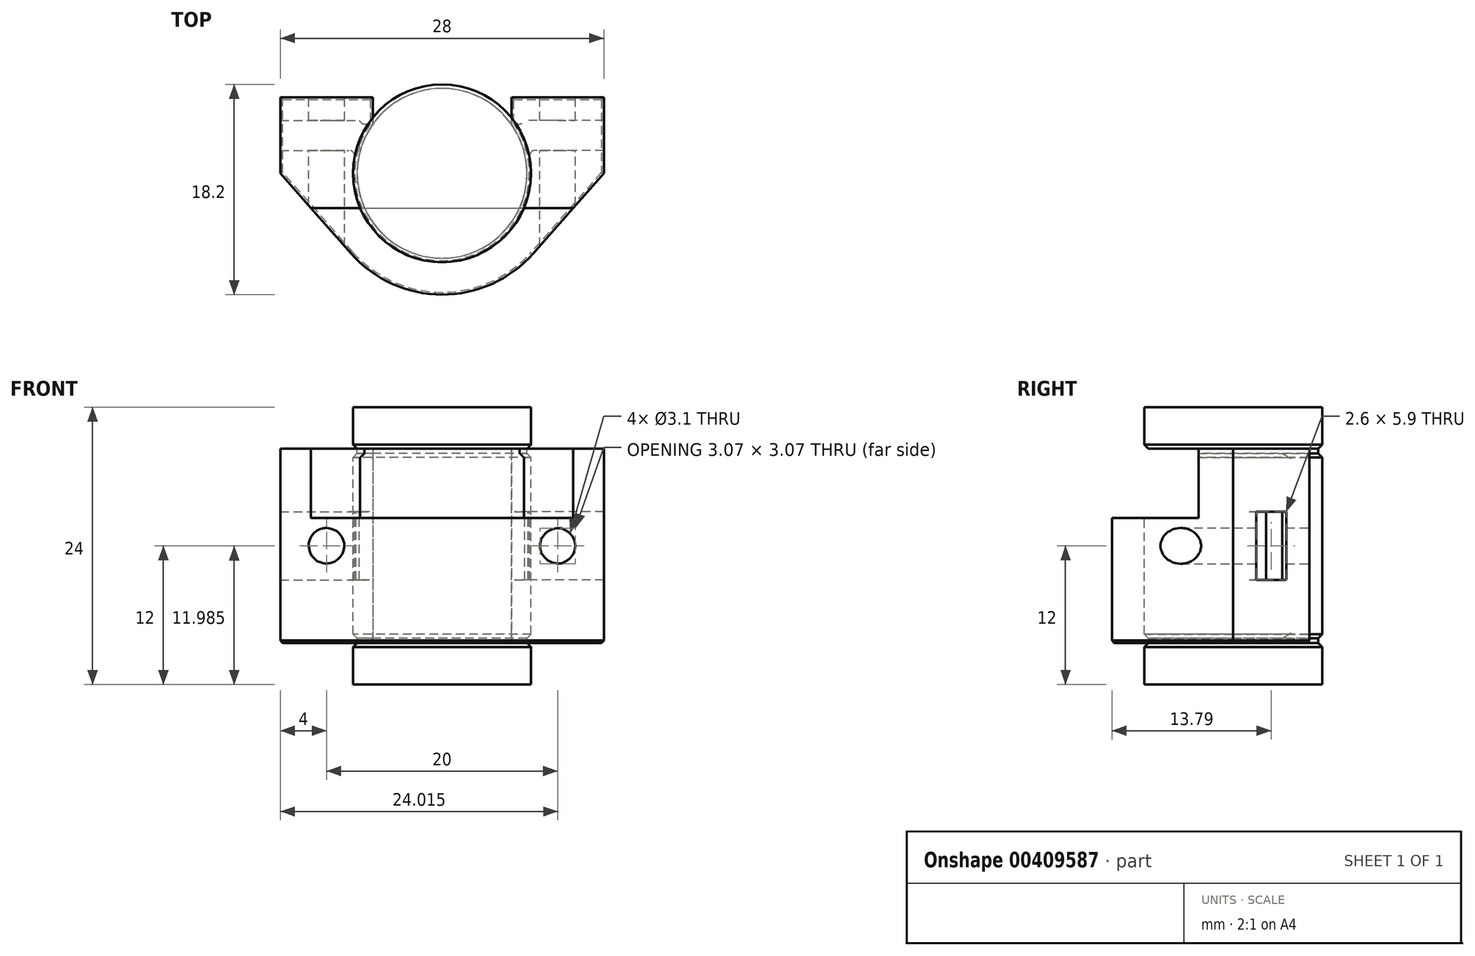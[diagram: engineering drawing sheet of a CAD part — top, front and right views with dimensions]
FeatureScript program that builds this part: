
annotation { "Feature Type Name" : "Feature", "Feature Type Description" : "" }
export const myFeature = defineFeature(function(context is Context, id is Id, definition is map)
    precondition{}
    {
        {
            var Q0;
            Q0=qCreatedBy(makeId("Front.planeOp"),FACE);
            var sketch = newSketch(context, id + "F0", { "sketchPlane" : qUnion([Q0])});
            skLineSegment(sketch, "E0", {"start": v(0, 12) * mm, "end": v(0, -12) * mm});
            skLineSegment(sketch, "E1.bottom", {"start": v(-4, 12) * mm, "end": v(-7.5, 12) * mm});
            skLineSegment(sketch, "E1.top", {"start": v(-4, -12) * mm, "end": v(-7.5, -12) * mm});
            skLineSegment(sketch, "E1.left", {"start": v(-4, 12) * mm, "end": v(-4, -12) * mm, "construction": true});
            skLineSegment(sketch, "E2", {"start": v(-7.5, 12) * mm, "end": v(-7.5, 8.75) * mm, "construction": true});
            skLineSegment(sketch, "E3", {"start": v(-7.5, 8.75) * mm, "end": v(-7.15, 8.75) * mm, "construction": true});
            skLineSegment(sketch, "E4", {"start": v(-7.15, 8.75) * mm, "end": v(-7.15, 7.65) * mm, "construction": true});
            skLineSegment(sketch, "E5", {"start": v(-7.15, 7.65) * mm, "end": v(-7.5, 7.65) * mm, "construction": true});
            skLineSegment(sketch, "E6", {"start": v(-7.5, 7.65) * mm, "end": v(-7.5, 0) * mm, "construction": true});
            skLineSegment(sketch, "E7.MirrorCS", {"start": v(-7.5, -8.75) * mm, "end": v(-7.15, -8.75) * mm, "construction": true});
            skLineSegment(sketch, "E8.MirrorCS", {"start": v(-7.15, -8.75) * mm, "end": v(-7.15, -7.65) * mm, "construction": true});
            skLineSegment(sketch, "E9.MirrorCS", {"start": v(-7.15, -7.65) * mm, "end": v(-7.5, -7.65) * mm, "construction": true});
            skLineSegment(sketch, "E10", {"start": v(-7.5, 0) * mm, "end": v(-7.5, -7.65) * mm, "construction": true});
            skLineSegment(sketch, "E11", {"start": v(-7.5, -8.75) * mm, "end": v(-7.5, -12) * mm, "construction": true});
            skLineSegment(sketch, "E12.0", {"start": v(-7.7, 12) * mm, "end": v(-7.7, 8.75) * mm});
            skLineSegment(sketch, "E13.0", {"start": v(-7.35, 8.75) * mm, "end": v(-7.35, 7.65) * mm});
            skLineSegment(sketch, "E14", {"start": v(-7.7, 8.75) * mm, "end": v(-7.35, 8.4) * mm});
            skLineSegment(sketch, "E15", {"start": v(-7.7, 7.65) * mm, "end": v(-7.7, 0) * mm});
            skLineSegment(sketch, "E16", {"start": v(-7.7, 7.65) * mm, "end": v(-7.35, 8) * mm});
            skLineSegment(sketch, "E17", {"start": v(-7.7, 12) * mm, "end": v(-7.5, 12) * mm});
            skLineSegment(sketch, "E18.MirrorCS", {"start": v(-7.7, -7.65) * mm, "end": v(-7.7, 0) * mm});
            skLineSegment(sketch, "E19.MirrorCS", {"start": v(-7.7, -7.65) * mm, "end": v(-7.35, -8) * mm});
            skLineSegment(sketch, "E20.MirrorCS", {"start": v(-7.35, -8.75) * mm, "end": v(-7.35, -7.65) * mm});
            skLineSegment(sketch, "E21.MirrorCS", {"start": v(-7.7, -8.75) * mm, "end": v(-7.35, -8.4) * mm});
            skLineSegment(sketch, "E22.MirrorCS", {"start": v(-7.7, -12) * mm, "end": v(-7.7, -8.75) * mm});
            skLineSegment(sketch, "E23.MirrorCS", {"start": v(-7.7, -12) * mm, "end": v(-7.5, -12) * mm});
            skLineSegment(sketch, "E24", {"start": v(-4, 12) * mm, "end": v(0, 12) * mm});
            skLineSegment(sketch, "E25", {"start": v(-4, -12) * mm, "end": v(0, -12) * mm});
            skSolve(sketch);
        }
        {
            var Q0;
            Q0=qCreatedBy(makeId("Top.planeOp"),FACE);
            var sketch = newSketch(context, id + "F1", { "sketchPlane" : qUnion([Q0])});
            skLineSegment(sketch, "E26", {"start": v(-5, 6.6) * mm, "end": v(5, 6.6) * mm, "construction": true});
            skCircle(sketch, "E27", {"center": v(0, 0) * mm, "radius": 7.5 * mm, "construction": true});
            skLineSegment(sketch, "E28", {"start": v(5, 6.6) * mm, "end": v(5, 5.6) * mm, "construction": true});
            skLineSegment(sketch, "E29", {"start": v(-5, 6.6) * mm, "end": v(-5, 5.6) * mm, "construction": true});
            skLineSegment(sketch, "E30", {"start": v(-5, 6.6) * mm, "end": v(-10, 6.6) * mm, "construction": true});
            skLineSegment(sketch, "E31", {"start": v(5, 6.6) * mm, "end": v(10, 6.6) * mm, "construction": true});
            skLineSegment(sketch, "E32", {"start": v(-10, 6.6) * mm, "end": v(-10, 4.6) * mm, "construction": true});
            skLineSegment(sketch, "E33.bottom", {"start": v(-12.85, 4.6) * mm, "end": v(-7.15, 4.6) * mm, "construction": true});
            skLineSegment(sketch, "E33.top", {"start": v(-12.85, 2) * mm, "end": v(-7.15, 2) * mm, "construction": true});
            skLineSegment(sketch, "E33.left", {"start": v(-12.85, 4.6) * mm, "end": v(-12.85, 2) * mm, "construction": true});
            skLineSegment(sketch, "E33.right", {"start": v(-7.15, 4.6) * mm, "end": v(-7.15, 2) * mm, "construction": true});
            skSolve(sketch);
        }
        {
            var Q0;
            Q0=qSketchRegion(id+"F0",true);
            var Q1;
            Q1=sQuery(id+"F0.wireOp",EDGE,"E0");
            revolve(context, id + "F2", {"entities" : qUnion([Q0]), "axis" : qUnion([Q1]), "revolveType" : RevolveType.FULL});
        }
        {
            var Q0;
            Q0=qCreatedBy(makeId("Top.planeOp"),FACE);
            var sketch = newSketch(context, id + "F3", { "sketchPlane" : qUnion([Q0])});
            skPoint(sketch, "E34.0", {"position": v(0, 6.6) * mm});
            skLineSegment(sketch, "E35", {"start": v(0, 6.6) * mm, "end": v(-14, 6.6) * mm, "construction": true});
            skLineSegment(sketch, "E36", {"start": v(-14, 6.6) * mm, "end": v(-14, 0) * mm});
            skLineSegment(sketch, "E37.MirrorCS", {"start": v(0, 6.6) * mm, "end": v(14, 6.6) * mm, "construction": true});
            skLineSegment(sketch, "E38.MirrorCS", {"start": v(14, 6.6) * mm, "end": v(14, 0) * mm});
            skCircle(sketch, "E39.0", {"center": v(0, 0) * mm, "radius": 7.5 * mm, "construction": true});
            skCircle(sketch, "E40.0", {"center": v(0, 0) * mm, "radius": 10.5 * mm, "construction": true});
            skArc(sketch, "E41", {"start": v(-7.88, -6.95) * mm, "mid": v(0, -10.5) * mm, "end": v(7.88, -6.95) * mm});
            skLineSegment(sketch, "E42", {"start": v(-14, 0) * mm, "end": v(-7.87, -6.95) * mm});
            skLineSegment(sketch, "E43.MirrorCS", {"start": v(14, 0) * mm, "end": v(7.87, -6.95) * mm});
            skLineSegment(sketch, "E44.0", {"start": v(-12.85, 4.6) * mm, "end": v(-7.15, 4.6) * mm, "construction": true});
            skLineSegment(sketch, "E45.0", {"start": v(-12.85, 2) * mm, "end": v(-7.15, 2) * mm, "construction": true});
            skLineSegment(sketch, "E46.0", {"start": v(-12.85, 4.6) * mm, "end": v(-12.85, 2) * mm, "construction": true});
            skLineSegment(sketch, "E47", {"start": v(-14, 6.6) * mm, "end": v(-6, 6.6) * mm});
            skLineSegment(sketch, "E48.MirrorCS", {"start": v(14, 6.6) * mm, "end": v(6, 6.6) * mm});
            skLineSegment(sketch, "E49.0", {"start": v(-7.15, 4.6) * mm, "end": v(-7.15, 2) * mm, "construction": true});
            skLineSegment(sketch, "E50", {"start": v(-6, 6.6) * mm, "end": v(-6, 3.3) * mm});
            skPoint(sketch, "E50.endSnap0", {"position": v(-7.15, 3.3) * mm});
            skLineSegment(sketch, "E51", {"start": v(-6, 3.3) * mm, "end": v(0, 3.3) * mm});
            skLineSegment(sketch, "E52.MirrorCS", {"start": v(6, 6.6) * mm, "end": v(6, 3.3) * mm});
            skLineSegment(sketch, "E53.MirrorCS", {"start": v(6, 3.3) * mm, "end": v(0, 3.3) * mm});
            skSolve(sketch);
        }
        {
            var Q0;
            Q0=qSketchRegion(id+"F3",true);
            var Q1;
            Q1=sQuery(id+"F0.wireOp",VERTEX,"E14.end");
            var Q2;
            Q2=sQuery(id+"F0.wireOp",VERTEX,"E21.MirrorCS.end");
            extrude(context, id + "F4", {"entities" : qUnion([Q0]), "endBound" : BoundingType.UP_TO_VERTEX, "endBoundEntityVertex" : qUnion([Q1]), "depth" : 25 * mm, "hasSecondDirection" : true, "secondDirectionBound" : BoundingType.UP_TO_VERTEX, "secondDirectionOppositeDirection" : true, "secondDirectionBoundEntityVertex" : qUnion([Q2]), "secondDirectionDepth" : 25 * mm});
        }
        {
            var Q0;
            Q0=makeQuery(id+"F4.opExtrude","SWEPT_FACE",FACE,{"disambiguationData":[OSD([sQuery(id+"F3.wireOp",EDGE,"E48.MirrorCS")])]});
            var sketch = newSketch(context, id + "F5", { "sketchPlane" : qUnion([Q0])});
            skPoint(sketch, "E54.0", {"position": v(-10, 0) * mm});
            skPoint(sketch, "E55.0", {"position": v(10, 0) * mm});
            skSolve(sketch);
        }
        {
            var Q0;
            Q0=makeQuery(id+"F2.opRevolve","SWEPT_BODY",BODY,{"disambiguationData":[OSD([sQuery(id+"F0.wireOp",EDGE,"E0"),sQuery(id+"F0.wireOp",EDGE,"E1.bottom"),sQuery(id+"F0.wireOp",EDGE,"E1.top"),sQuery(id+"F0.wireOp",EDGE,"E12.0"),sQuery(id+"F0.wireOp",EDGE,"E13.0"),sQuery(id+"F0.wireOp",EDGE,"E14"),sQuery(id+"F0.wireOp",EDGE,"E15"),sQuery(id+"F0.wireOp",EDGE,"E16"),sQuery(id+"F0.wireOp",EDGE,"E17"),sQuery(id+"F0.wireOp",EDGE,"E18.MirrorCS"),sQuery(id+"F0.wireOp",EDGE,"E19.MirrorCS"),sQuery(id+"F0.wireOp",EDGE,"E20.MirrorCS"),sQuery(id+"F0.wireOp",EDGE,"E21.MirrorCS"),sQuery(id+"F0.wireOp",EDGE,"E22.MirrorCS"),sQuery(id+"F0.wireOp",EDGE,"E23.MirrorCS"),sQuery(id+"F0.wireOp",EDGE,"E24"),sQuery(id+"F0.wireOp",EDGE,"E25")])]});
            var Q1;
            Q1=makeQuery(id+"F4.opExtrude","SWEPT_BODY",BODY,{"disambiguationData":[OSD([sQuery(id+"F3.wireOp",EDGE,"E36"),sQuery(id+"F3.wireOp",EDGE,"E38.MirrorCS"),sQuery(id+"F3.wireOp",EDGE,"E41"),sQuery(id+"F3.wireOp",EDGE,"E42"),sQuery(id+"F3.wireOp",EDGE,"E43.MirrorCS"),sQuery(id+"F3.wireOp",EDGE,"E47"),sQuery(id+"F3.wireOp",EDGE,"E48.MirrorCS"),sQuery(id+"F3.wireOp",EDGE,"E50"),sQuery(id+"F3.wireOp",EDGE,"E51"),sQuery(id+"F3.wireOp",EDGE,"E52.MirrorCS"),sQuery(id+"F3.wireOp",EDGE,"E53.MirrorCS")])]});
            booleanBodies(context, id + "F6", {"operationType" : BooleanOperationType.SUBTRACTION, "tools" : qUnion([Q0]), "targets" : qUnion([Q1]), "keepTools" : true});
        }
        {
            var Q0;
            Q0=sQuery(id+"F5.wireOp",VERTEX,"E54.0");
            var Q1;
            Q1=sQuery(id+"F5.wireOp",VERTEX,"E55.0");
            var Q2;
            Q2=makeQuery(id+"F4.opExtrude","SWEPT_BODY",BODY,{"disambiguationData":[OSD([sQuery(id+"F3.wireOp",EDGE,"E36"),sQuery(id+"F3.wireOp",EDGE,"E38.MirrorCS"),sQuery(id+"F3.wireOp",EDGE,"E41"),sQuery(id+"F3.wireOp",EDGE,"E42"),sQuery(id+"F3.wireOp",EDGE,"E43.MirrorCS"),sQuery(id+"F3.wireOp",EDGE,"E47"),sQuery(id+"F3.wireOp",EDGE,"E48.MirrorCS"),sQuery(id+"F3.wireOp",EDGE,"E50"),sQuery(id+"F3.wireOp",EDGE,"E51"),sQuery(id+"F3.wireOp",EDGE,"E52.MirrorCS"),sQuery(id+"F3.wireOp",EDGE,"E53.MirrorCS")])]});
            hole(context, id + "F7", {"style" : HoleStyle.SIMPLE, "endStyle" : HoleEndStyle.THROUGH, "holeDiameter" : 3.1 * mm, "isTappedThrough" : true, "tappedDepth" : 12 * mm, "tapClearance" : 3, "locations" : qUnion([Q0, Q1]), "scope" : qUnion([Q2])});
        }
        {
            var Q0;
            Q0=qCreatedBy(makeId("Top.planeOp"),FACE);
            var sketch = newSketch(context, id + "F8", { "sketchPlane" : qUnion([Q0])});
            skLineSegment(sketch, "E56.0", {"start": v(-12.85, 2) * mm, "end": v(-7.15, 2) * mm});
            skLineSegment(sketch, "E57.0", {"start": v(-12.85, 4.6) * mm, "end": v(-12.85, 2) * mm, "construction": true});
            skLineSegment(sketch, "E58.0", {"start": v(-12.85, 4.6) * mm, "end": v(-7.15, 4.6) * mm});
            skLineSegment(sketch, "E59.0", {"start": v(-7.15, 4.6) * mm, "end": v(-7.15, 2) * mm});
            skLineSegment(sketch, "E60.MirrorCS", {"start": v(12.85, 4.6) * mm, "end": v(7.15, 4.6) * mm});
            skLineSegment(sketch, "E61.MirrorCS", {"start": v(12.85, 4.6) * mm, "end": v(12.85, 2) * mm, "construction": true});
            skLineSegment(sketch, "E62.MirrorCS", {"start": v(12.85, 2) * mm, "end": v(7.15, 2) * mm});
            skLineSegment(sketch, "E63.MirrorCS", {"start": v(7.15, 4.6) * mm, "end": v(7.15, 2) * mm});
            skLineSegment(sketch, "E64", {"start": v(-12.85, 4.6) * mm, "end": v(-19.02, 4.6) * mm});
            skLineSegment(sketch, "E65", {"start": v(-19.02, 4.6) * mm, "end": v(-19.02, 2) * mm});
            skLineSegment(sketch, "E66", {"start": v(-19.02, 2) * mm, "end": v(-12.85, 2) * mm});
            skLineSegment(sketch, "E67.MirrorCS", {"start": v(12.85, 4.6) * mm, "end": v(19.02, 4.6) * mm});
            skLineSegment(sketch, "E68.MirrorCS", {"start": v(19.02, 4.6) * mm, "end": v(19.02, 2) * mm});
            skLineSegment(sketch, "E69.MirrorCS", {"start": v(19.02, 2) * mm, "end": v(12.85, 2) * mm});
            skSolve(sketch);
        }
        {
            var Q0;
            Q0=qSketchRegion(id+"F8",true);
            extrude(context, id + "F9", {"entities" : qUnion([Q0]), "operationType" : NewBodyOperationType.REMOVE, "depth" : (0.4 + 5.5) * mm, "symmetric" : true});
        }
        {
            var Q0;
            Q0=makeQuery(id+"F4.opExtrude","TWEAK_EDGE",EDGE,{"derivedFrom":[makeQuery(id+"F3.imprint","IMPRINT",EDGE,{"derivedFrom":sQuery(id+"F3.wireOp",EDGE,"E47")}),makeQuery(id+"F3.imprint","IMPRINT",EDGE,{"derivedFrom":sQuery(id+"F3.wireOp",EDGE,"E50")})]});
            var Q1;
            Q1=makeQuery(id+"F4.opExtrude","TWEAK_EDGE",EDGE,{"derivedFrom":[makeQuery(id+"F3.imprint","IMPRINT",EDGE,{"derivedFrom":sQuery(id+"F3.wireOp",EDGE,"E36")}),makeQuery(id+"F3.imprint","IMPRINT",EDGE,{"derivedFrom":sQuery(id+"F3.wireOp",EDGE,"E47")})]});
            var Q2;
            Q2=makeQuery(id+"F4.opExtrude","TWEAK_EDGE",EDGE,{"derivedFrom":[makeQuery(id+"F3.imprint","IMPRINT",EDGE,{"derivedFrom":sQuery(id+"F3.wireOp",EDGE,"E48.MirrorCS")}),makeQuery(id+"F3.imprint","IMPRINT",EDGE,{"derivedFrom":sQuery(id+"F3.wireOp",EDGE,"E52.MirrorCS")})]});
            var Q3;
            Q3=makeQuery(id+"F4.opExtrude","TWEAK_EDGE",EDGE,{"derivedFrom":[makeQuery(id+"F3.imprint","IMPRINT",EDGE,{"derivedFrom":sQuery(id+"F3.wireOp",EDGE,"E38.MirrorCS")}),makeQuery(id+"F3.imprint","IMPRINT",EDGE,{"derivedFrom":sQuery(id+"F3.wireOp",EDGE,"E48.MirrorCS")})]});
            var Q4;
            Q4=makeQuery(id+"F6.opBoolean","INTERSECT",EDGE,{"derivedFrom":[makeQuery(id+"F2.opRevolve","SWEPT_FACE",FACE,{"disambiguationData":[OSD([sQuery(id+"F0.wireOp",EDGE,"E15"),sQuery(id+"F0.wireOp",EDGE,"E18.MirrorCS")])]}),makeQuery(id+"F4.opExtrude","SWEPT_FACE",FACE,{"disambiguationData":[OSD([sQuery(id+"F3.wireOp",EDGE,"E52.MirrorCS")])]})]});
            var Q5;
            Q5=makeQuery(id+"F6.opBoolean","INTERSECT",EDGE,{"derivedFrom":[makeQuery(id+"F2.opRevolve","SWEPT_FACE",FACE,{"disambiguationData":[OSD([sQuery(id+"F0.wireOp",EDGE,"E15"),sQuery(id+"F0.wireOp",EDGE,"E18.MirrorCS")])]}),makeQuery(id+"F4.opExtrude","SWEPT_FACE",FACE,{"disambiguationData":[OSD([sQuery(id+"F3.wireOp",EDGE,"E50")])]})]});
            var Q6;
            Q6=makeQuery(id+"F6.opBoolean","INTERSECT",EDGE,{"derivedFrom":[makeQuery(id+"F2.opRevolve","SWEPT_FACE",FACE,{"disambiguationData":[OSD([sQuery(id+"F0.wireOp",EDGE,"E13.0")])]}),makeQuery(id+"F4.opExtrude","SWEPT_FACE",FACE,{"disambiguationData":[OSD([sQuery(id+"F3.wireOp",EDGE,"E50")])]})]});
            var Q7;
            Q7=makeQuery(id+"F6.opBoolean","INTERSECT",EDGE,{"derivedFrom":[makeQuery(id+"F2.opRevolve","SWEPT_FACE",FACE,{"disambiguationData":[OSD([sQuery(id+"F0.wireOp",EDGE,"E20.MirrorCS")])]}),makeQuery(id+"F4.opExtrude","SWEPT_FACE",FACE,{"disambiguationData":[OSD([sQuery(id+"F3.wireOp",EDGE,"E50")])]})]});
            var Q8;
            Q8=makeQuery(id+"F6.opBoolean","INTERSECT",EDGE,{"derivedFrom":[makeQuery(id+"F2.opRevolve","SWEPT_FACE",FACE,{"disambiguationData":[OSD([sQuery(id+"F0.wireOp",EDGE,"E13.0")])]}),makeQuery(id+"F4.opExtrude","SWEPT_FACE",FACE,{"disambiguationData":[OSD([sQuery(id+"F3.wireOp",EDGE,"E52.MirrorCS")])]})]});
            var Q9;
            Q9=makeQuery(id+"F6.opBoolean","INTERSECT",EDGE,{"derivedFrom":[makeQuery(id+"F2.opRevolve","SWEPT_FACE",FACE,{"disambiguationData":[OSD([sQuery(id+"F0.wireOp",EDGE,"E20.MirrorCS")])]}),makeQuery(id+"F4.opExtrude","SWEPT_FACE",FACE,{"disambiguationData":[OSD([sQuery(id+"F3.wireOp",EDGE,"E52.MirrorCS")])]})]});
            var Q10;
            Q10=makeQuery(id+"F4.opExtrude","TWEAK_EDGE",EDGE,{"derivedFrom":[makeQuery(id+"F3.imprint","IMPRINT",EDGE,{"derivedFrom":sQuery(id+"F3.wireOp",EDGE,"E36")}),makeQuery(id+"F3.imprint","IMPRINT",EDGE,{"derivedFrom":sQuery(id+"F3.wireOp",EDGE,"E42")})]});
            var Q11;
            Q11=makeQuery(id+"F4.opExtrude","TWEAK_EDGE",EDGE,{"derivedFrom":[makeQuery(id+"F3.imprint","IMPRINT",EDGE,{"derivedFrom":sQuery(id+"F3.wireOp",EDGE,"E38.MirrorCS")}),makeQuery(id+"F3.imprint","IMPRINT",EDGE,{"derivedFrom":sQuery(id+"F3.wireOp",EDGE,"E43.MirrorCS")})]});
            var Q12;
            Q12=makeQuery(id+"F9.boolean.opBoolean","INTERSECT",EDGE,{"derivedFrom":[makeQuery(id+"F6.opBoolean","COPY",FACE,{"derivedFrom":makeQuery(id+"F2.opRevolve","SWEPT_FACE",FACE,{"disambiguationData":[OSD([sQuery(id+"F0.wireOp",EDGE,"E15"),sQuery(id+"F0.wireOp",EDGE,"E18.MirrorCS")])]})}),makeQuery(id+"F9.opExtrude","SWEPT_FACE",FACE,{"disambiguationData":[OSD([sQuery(id+"F8.wireOp",EDGE,"E59.0")])]})]});
            var Q13;
            Q13=makeQuery(id+"F9.boolean.opBoolean","INTERSECT",EDGE,{"derivedFrom":[makeQuery(id+"F6.opBoolean","COPY",FACE,{"derivedFrom":makeQuery(id+"F2.opRevolve","SWEPT_FACE",FACE,{"disambiguationData":[OSD([sQuery(id+"F0.wireOp",EDGE,"E15"),sQuery(id+"F0.wireOp",EDGE,"E18.MirrorCS")])]})}),makeQuery(id+"F9.opExtrude","SWEPT_FACE",FACE,{"disambiguationData":[OSD([sQuery(id+"F8.wireOp",EDGE,"E63.MirrorCS")])]})]});
            var Q14;
            Q14=makeQuery(id+"F9.boolean.opBoolean","INTERSECT",EDGE,{"derivedFrom":[makeQuery(id+"F6.opBoolean","COPY",FACE,{"derivedFrom":makeQuery(id+"F2.opRevolve","SWEPT_FACE",FACE,{"disambiguationData":[OSD([sQuery(id+"F0.wireOp",EDGE,"E15"),sQuery(id+"F0.wireOp",EDGE,"E18.MirrorCS")])]})}),makeQuery(id+"F9.opExtrude","SWEPT_FACE",FACE,{"disambiguationData":[OSD([sQuery(id+"F8.wireOp",EDGE,"E56.0"),sQuery(id+"F8.wireOp",EDGE,"E66")])]})]});
            var Q15;
            Q15=makeQuery(id+"F9.boolean.opBoolean","INTERSECT",EDGE,{"derivedFrom":[makeQuery(id+"F6.opBoolean","COPY",FACE,{"derivedFrom":makeQuery(id+"F2.opRevolve","SWEPT_FACE",FACE,{"disambiguationData":[OSD([sQuery(id+"F0.wireOp",EDGE,"E15"),sQuery(id+"F0.wireOp",EDGE,"E18.MirrorCS")])]})}),makeQuery(id+"F9.opExtrude","SWEPT_FACE",FACE,{"disambiguationData":[OSD([sQuery(id+"F8.wireOp",EDGE,"E62.MirrorCS"),sQuery(id+"F8.wireOp",EDGE,"E69.MirrorCS")])]})]});
            fillet(context, id + "F10", {"entities" : qUnion([Q0, Q1, Q2, Q3, Q4, Q5, Q6, Q7, Q8, Q9, Q10, Q11, Q12, Q13, Q14, Q15]), "radius" : .5 * mm, "allowEdgeOverflow" : false});
        }
        {
            var Q0;
            Q0=makeQuery(id+"F4.opExtrude","CAP_FACE",FACE,{"disambiguationData":[OSD([sQuery(id+"F3.wireOp",EDGE,"E36"),sQuery(id+"F3.wireOp",EDGE,"E38.MirrorCS"),sQuery(id+"F3.wireOp",EDGE,"E41"),sQuery(id+"F3.wireOp",EDGE,"E42"),sQuery(id+"F3.wireOp",EDGE,"E43.MirrorCS"),sQuery(id+"F3.wireOp",EDGE,"E47"),sQuery(id+"F3.wireOp",EDGE,"E48.MirrorCS"),sQuery(id+"F3.wireOp",EDGE,"E50"),sQuery(id+"F3.wireOp",EDGE,"E51"),sQuery(id+"F3.wireOp",EDGE,"E52.MirrorCS"),sQuery(id+"F3.wireOp",EDGE,"E53.MirrorCS")])],"isStart":true});
            chamfer(context, id + "F11", {"entities" : qUnion([Q0]), "width" : .2 * mm});
        }
        {
            var Q0;
            Q0=makeQuery(id+"F4.opExtrude","CAP_FACE",FACE,{"disambiguationData":[OSD([sQuery(id+"F3.wireOp",EDGE,"E36"),sQuery(id+"F3.wireOp",EDGE,"E38.MirrorCS"),sQuery(id+"F3.wireOp",EDGE,"E41"),sQuery(id+"F3.wireOp",EDGE,"E42"),sQuery(id+"F3.wireOp",EDGE,"E43.MirrorCS"),sQuery(id+"F3.wireOp",EDGE,"E47"),sQuery(id+"F3.wireOp",EDGE,"E48.MirrorCS"),sQuery(id+"F3.wireOp",EDGE,"E50"),sQuery(id+"F3.wireOp",EDGE,"E51"),sQuery(id+"F3.wireOp",EDGE,"E52.MirrorCS"),sQuery(id+"F3.wireOp",EDGE,"E53.MirrorCS")])],"isStart":false});
            var sketch = newSketch(context, id + "F12", { "sketchPlane" : qUnion([Q0])});
            skCircle(sketch, "E70.0", {"center": v(0, 0) * mm, "radius": 7.5 * mm, "construction": true});
            skLineSegment(sketch, "E71", {"start": v(0, -7.5) * mm, "end": v(0, -3) * mm, "construction": true});
            skLineSegment(sketch, "E72.bottom", {"start": v(-29.21, -15.23) * mm, "end": v(29.21, -15.23) * mm});
            skLineSegment(sketch, "E72.top", {"start": v(-29.21, -3) * mm, "end": v(29.21, -3) * mm});
            skLineSegment(sketch, "E72.left", {"start": v(-29.21, -15.23) * mm, "end": v(-29.21, -3) * mm});
            skLineSegment(sketch, "E72.right", {"start": v(29.21, -15.23) * mm, "end": v(29.21, -3) * mm});
            skSolve(sketch);
        }
        {
            var Q0;
            Q0 = qSketchRegion(id + "F12", true);
            extrude(context, id + "F13", {"entities" : qUnion([Q0]), "operationType" : NewBodyOperationType.REMOVE, "oppositeDirection" : true, "depth" : 6 * mm});
        }
    });
